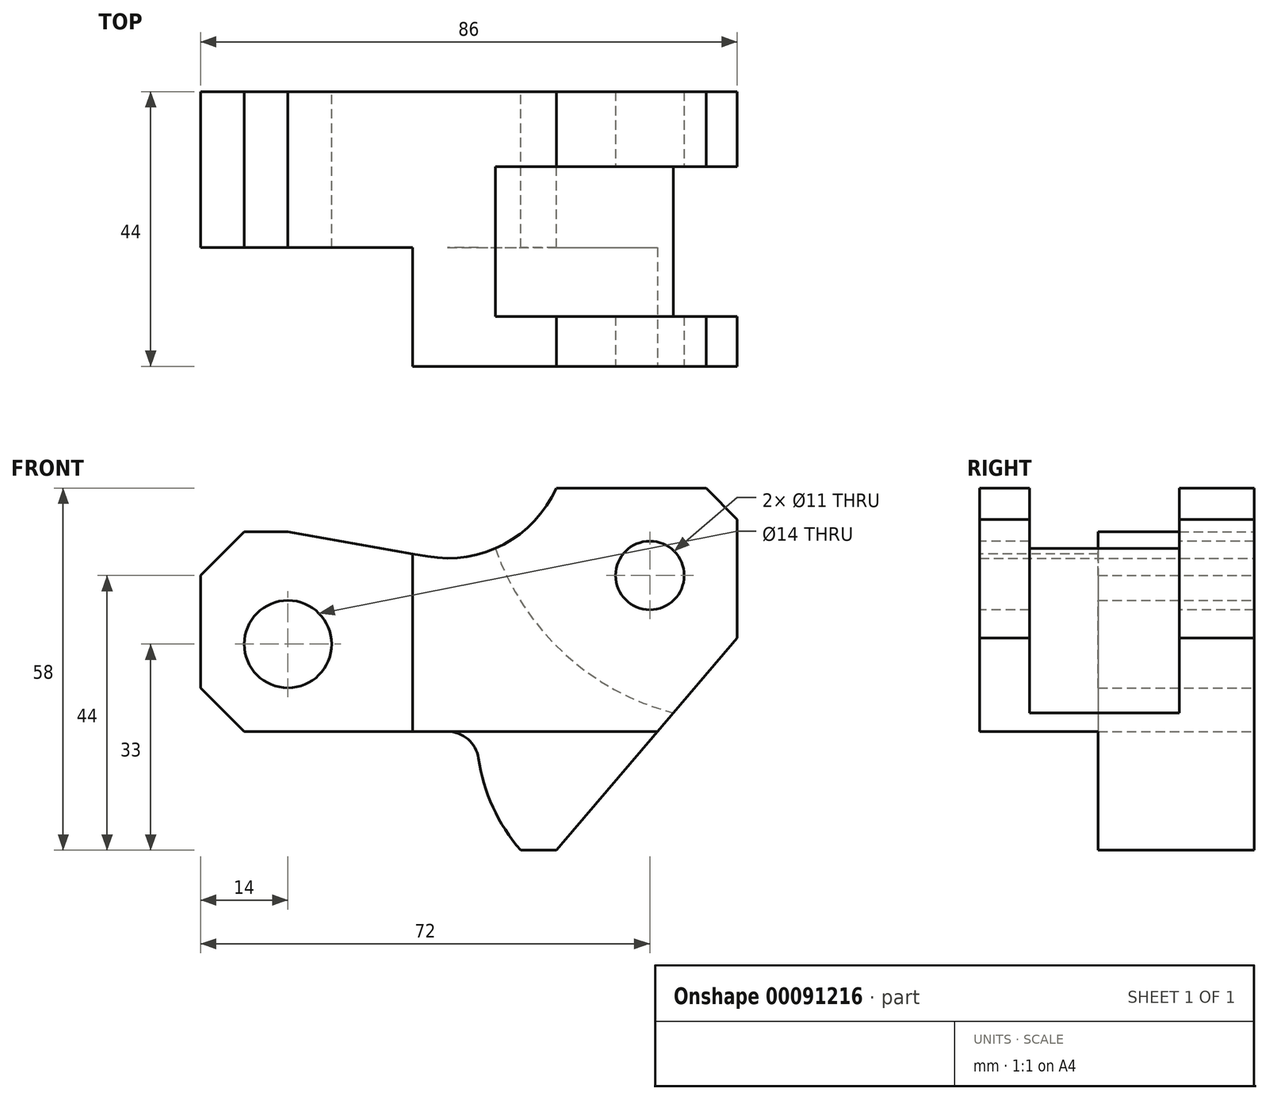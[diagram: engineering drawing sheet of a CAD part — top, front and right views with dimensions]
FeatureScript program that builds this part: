
annotation { "Feature Type Name" : "Feature", "Feature Type Description" : "" }
export const myFeature = defineFeature(function(context is Context, id is Id, definition is map)
    precondition{}
    {
        {
            var Q0;
            Q0=qCreatedBy(makeId("Front.planeOp"),FACE);
            var sketch = newSketch(context, id + "F0", { "sketchPlane" : qUnion([Q0])});
            skCircle(sketch, "E0", {"center": v(0, 0) * mm, "radius": 7 * mm});
            skLineSegment(sketch, "E1", {"start": v(-14, 11) * mm, "end": v(-14, -7) * mm});
            skLineSegment(sketch, "E2", {"start": v(25.58, -14) * mm, "end": v(-7, -14) * mm});
            skLineSegment(sketch, "E3", {"start": v(-14, -7) * mm, "end": v(-7, -14) * mm});
            skLineSegment(sketch, "E4", {"start": v(-7, 18) * mm, "end": v(0, 18) * mm});
            skLineSegment(sketch, "E5", {"start": v(-14, 11) * mm, "end": v(-7, 18) * mm});
            skLineSegment(sketch, "E6", {"start": v(0, 18) * mm, "end": v(22.36, 14.06) * mm});
            skLineSegment(sketch, "E7", {"start": v(67, 25) * mm, "end": v(43, 25) * mm});
            skLineSegment(sketch, "E8", {"start": v(67, 25) * mm, "end": v(72, 20) * mm});
            skLineSegment(sketch, "E9", {"start": v(72, 20) * mm, "end": v(72, 1) * mm});
            skLineSegment(sketch, "E10", {"start": v(43, -33) * mm, "end": v(37.3, -33) * mm});
            skArc(sketch, "E11", {"start": v(22.36, 14.06) * mm, "mid": v(34.56, 15.98) * mm, "end": v(43, 25) * mm});
            skArc(sketch, "E12", {"start": v(25.58, -14) * mm, "mid": v(28.84, -15.21) * mm, "end": v(30.52, -18.26) * mm});
            skLineSegment(sketch, "E13", {"start": v(43, -33) * mm, "end": v(72, 1) * mm});
            skArc(sketch, "E14", {"start": v(30.52, -18.26) * mm, "mid": v(32.86, -26.12) * mm, "end": v(37.3, -33) * mm});
            skLineSegment(sketch, "E15", {"start": v(25.58, -14) * mm, "end": v(59.2, -14) * mm, "construction": true});
            skLineSegment(sketch, "E16", {"start": v(20, 14.47) * mm, "end": v(20, -14) * mm, "construction": true});
            skSolve(sketch);
        }
        {
            var Q0;
            Q0=makeQuery(id+"F0.imprint","IMPRINT",FACE,{"disambiguationData":[TD([[makeQuery(id+"F0.imprint","IMPRINT",EDGE,{"derivedFrom":sQuery(id+"F0.wireOp",EDGE,"E0")}),-1.0]])]});
            extrude(context, id + "F1", {"entities" : qUnion([Q0]), "endBound" : BoundingType.SYMMETRIC, "depth" : 44 * mm});
        }
        {
            var Q0;
            Q0=makeQuery(id+"F1.opExtrude","CAP_FACE",FACE,{"disambiguationData":[OSD([sQuery(id+"F0.wireOp",EDGE,"E0"),sQuery(id+"F0.wireOp",EDGE,"E1"),sQuery(id+"F0.wireOp",EDGE,"E2"),sQuery(id+"F0.wireOp",EDGE,"E3"),sQuery(id+"F0.wireOp",EDGE,"E4"),sQuery(id+"F0.wireOp",EDGE,"E5"),sQuery(id+"F0.wireOp",EDGE,"E6"),sQuery(id+"F0.wireOp",EDGE,"E7"),sQuery(id+"F0.wireOp",EDGE,"E8"),sQuery(id+"F0.wireOp",EDGE,"E9"),sQuery(id+"F0.wireOp",EDGE,"E10"),sQuery(id+"F0.wireOp",EDGE,"E11"),sQuery(id+"F0.wireOp",EDGE,"E12"),sQuery(id+"F0.wireOp",EDGE,"E13"),sQuery(id+"F0.wireOp",EDGE,"E14")])],"isStart":false});
            var sketch = newSketch(context, id + "F2", { "sketchPlane" : qUnion([Q0])});
            skLineSegment(sketch, "E17", {"start": v(20, 14.47) * mm, "end": v(20, -14) * mm});
            skLineSegment(sketch, "E18", {"start": v(25.58, -14) * mm, "end": v(59.2, -14) * mm});
            skCircle(sketch, "E19", {"center": v(58, 11) * mm, "radius": 5.5 * mm});
            skSolve(sketch);
        }
        {
            var Q0;
            {var subQ3=sQuery(id+"F2.wireOp",EDGE,"E17");Q0=makeQuery(id+"F2.imprint","IMPRINT",FACE,{"disambiguationData":[TD([[makeQuery(id+"F2.imprint","IMPRINT",EDGE,{"derivedFrom":subQ3}),-1.0]])]});}
            var Q1;
            {var subQ1=sQuery(id+"F2.wireOp",EDGE,"E18");Q1=makeQuery(id+"F2.imprint","IMPRINT",FACE,{"disambiguationData":[TD([[makeQuery(id+"F2.imprint","IMPRINT",EDGE,{"derivedFrom":subQ1}),-1.0]])]});}
            extrude(context, id + "F3", {"entities" : qUnion([Q0, Q1]), "operationType" : NewBodyOperationType.REMOVE, "oppositeDirection" : true, "depth" : 19 * mm});
        }
        {
            var Q0;
            Q0=makeQuery(id+"F2.imprint","IMPRINT",FACE,{"disambiguationData":[TD([[makeQuery(id+"F2.imprint","IMPRINT",EDGE,{"derivedFrom":sQuery(id+"F2.wireOp",EDGE,"E19")}),1.0]])]});
            extrude(context, id + "F4", {"entities" : qUnion([Q0]), "operationType" : NewBodyOperationType.REMOVE, "endBound" : BoundingType.THROUGH_ALL, "oppositeDirection" : true, "depth" : 25 * mm});
        }
        {
            var Q0;
            Q0=qCreatedBy(makeId("Front.planeOp"),FACE);
            cPlane(context, id + "F5", {"entities" : qUnion([Q0]), "cplaneType" : CPlaneType.OFFSET, "offset" : 10 * mm, "oppositeDirection" : true, "width" : 150 * mm, "height" : 150 * mm});
        }
        {
            var Q0;
            Q0=qCreatedBy(id+"F5.planeOp",FACE);
            var sketch = newSketch(context, id + "F6", { "sketchPlane" : qUnion([Q0])});
            skArc(sketch, "E20", {"start": v(31.04, 26.91) * mm, "mid": v(40.15, 2.89) * mm, "end": v(61.76, -11) * mm});
            skLineSegment(sketch, "E21", {"start": v(72, 34.15) * mm, "end": v(72, 12.44) * mm, "construction": true});
            skLineSegment(sketch, "E22", {"start": v(72, 26.53) * mm, "end": v(72, 0) * mm});
            skLineSegment(sketch, "E23", {"start": v(72, 25) * mm, "end": v(31.04, 25) * mm});
            skLineSegment(sketch, "E24", {"start": v(72, 0) * mm, "end": v(61.76, -11) * mm});
            skSolve(sketch);
        }
        {
            var Q0;
            Q0 = qSketchRegion(id + "F6", true);
            extrude(context, id + "F7", {"entities" : qUnion([Q0]), "operationType" : NewBodyOperationType.REMOVE, "depth" : 24 * mm});
        }
    });
